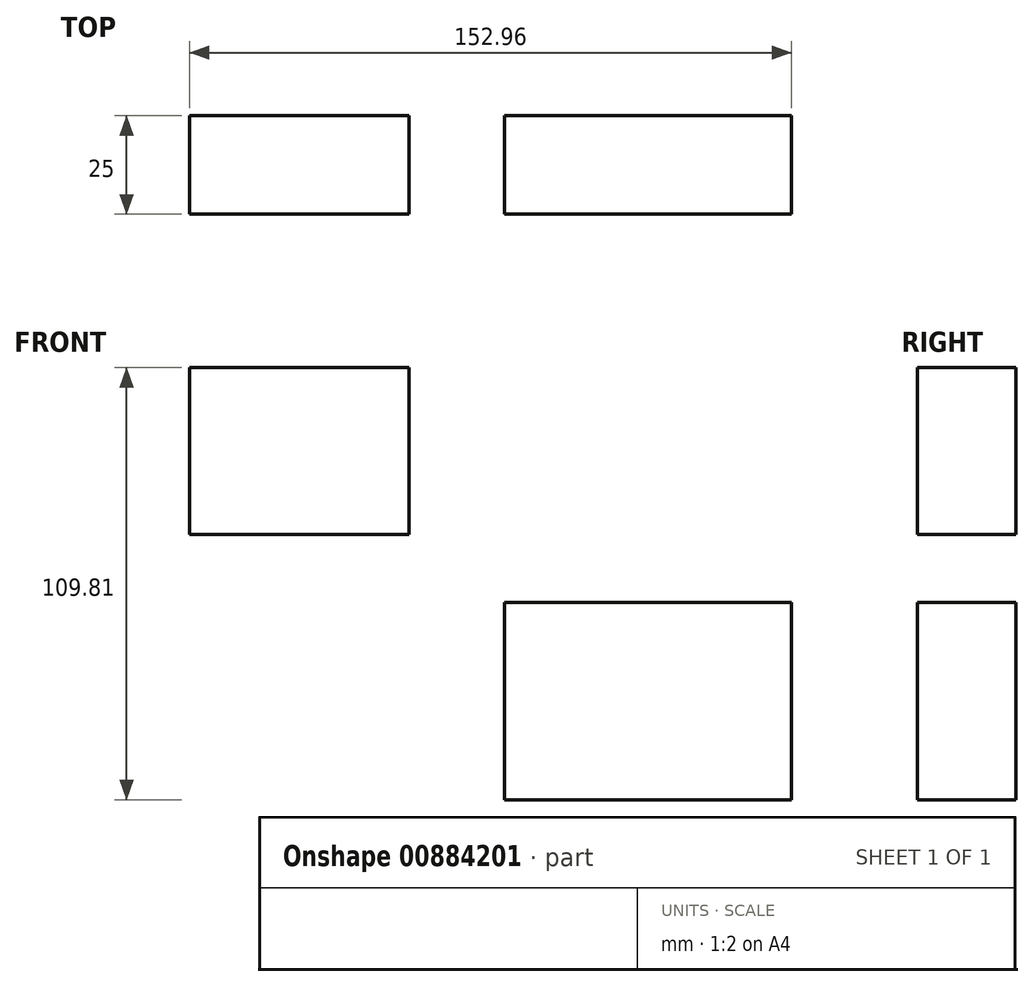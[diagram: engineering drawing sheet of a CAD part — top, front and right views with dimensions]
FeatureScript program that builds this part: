
annotation { "Feature Type Name" : "Feature", "Feature Type Description" : "" }
export const myFeature = defineFeature(function(context is Context, id is Id, definition is map)
    precondition{}
    {
        {
            var Q0;
            Q0=qCreatedBy(makeId("Front.planeOp"),FACE);
            var sketch = newSketch(context, id + "F0", { "sketchPlane" : qUnion([Q0])});
            skLineSegment(sketch, "E0.bottom", {"start": v(-134.98, 54.33) * mm, "end": v(-79.84, 54.33) * mm});
            skLineSegment(sketch, "E0.top", {"start": v(-134.98, 16.79) * mm, "end": v(-79.84, 16.79) * mm});
            skLineSegment(sketch, "E0.left", {"start": v(-134.98, 54.33) * mm, "end": v(-134.98, 16.79) * mm});
            skLineSegment(sketch, "E0.right", {"start": v(-79.84, 54.33) * mm, "end": v(-79.84, 16.79) * mm});
            skLineSegment(sketch, "E1.bottom", {"start": v(-31.77, 38.4) * mm, "end": v(24.04, 38.4) * mm});
            skLineSegment(sketch, "E1.top", {"start": v(-31.77, -3.99) * mm, "end": v(24.04, -3.99) * mm});
            skLineSegment(sketch, "E1.left", {"start": v(-31.77, 38.4) * mm, "end": v(-31.77, -3.99) * mm});
            skLineSegment(sketch, "E1.right", {"start": v(24.04, 38.4) * mm, "end": v(24.04, -3.99) * mm});
            skLineSegment(sketch, "E2.bottom", {"start": v(48.24, -21.2) * mm, "end": v(121.2, -21.2) * mm});
            skLineSegment(sketch, "E2.top", {"start": v(48.24, -71.41) * mm, "end": v(121.2, -71.41) * mm});
            skLineSegment(sketch, "E2.left", {"start": v(48.24, -21.2) * mm, "end": v(48.24, -71.41) * mm});
            skLineSegment(sketch, "E2.right", {"start": v(121.2, -21.2) * mm, "end": v(121.2, -71.41) * mm});
            skSolve(sketch);
        }
        {
            var Q0;
            Q0=makeQuery(id+"F0.imprint","IMPRINT",FACE,{"disambiguationData":[TD([[makeQuery(id+"F0.imprint","IMPRINT",EDGE,{"derivedFrom":sQuery(id+"F0.wireOp",EDGE,"E2.bottom")}),-1.0]])]});
            extrude(context, id + "F1", {"entities" : qUnion([Q0]), "depth" : 25 * mm, "offsetDistance" : 25 * mm});
        }
        {
            var Q0;
            Q0=makeQuery(id+"F0.imprint","IMPRINT",FACE,{"disambiguationData":[TD([[makeQuery(id+"F0.imprint","IMPRINT",EDGE,{"derivedFrom":sQuery(id+"F0.wireOp",EDGE,"E1.bottom")}),-1.0]])]});
            extrude(context, id + "F2", {"entities" : qUnion([Q0]), "depth" : 25 * mm, "offsetDistance" : 25 * mm});
        }
    });
